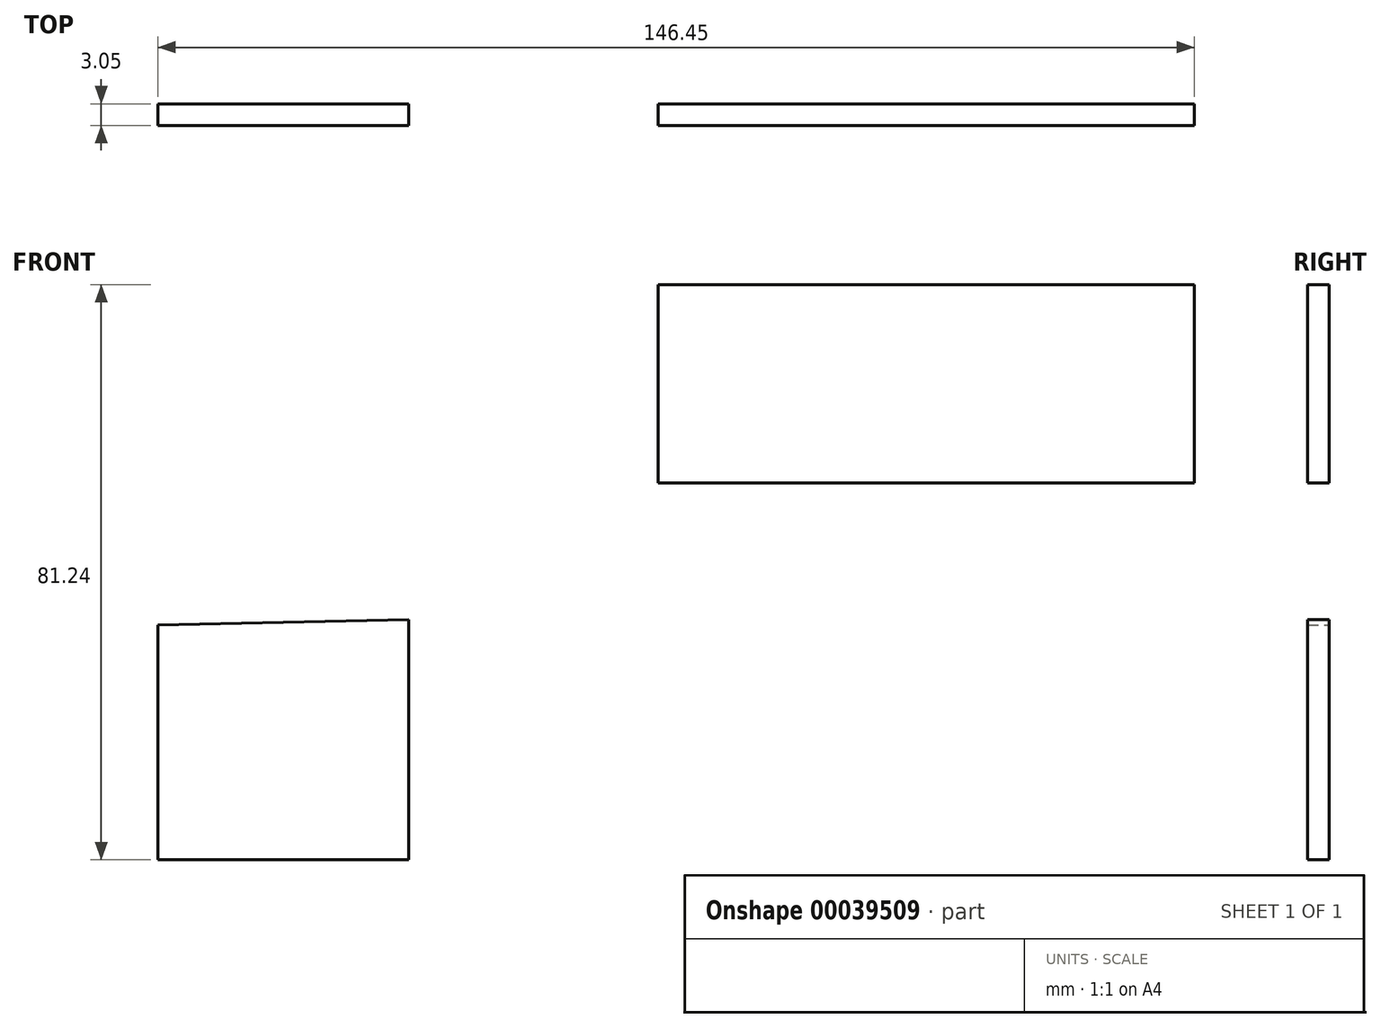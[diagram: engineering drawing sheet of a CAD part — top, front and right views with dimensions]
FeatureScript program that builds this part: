
annotation { "Feature Type Name" : "Feature", "Feature Type Description" : "" }
export const myFeature = defineFeature(function(context is Context, id is Id, definition is map)
    precondition{}
    {
        {
            var Q0;
            Q0=qCreatedBy(makeId("Front.planeOp"),FACE);
            var sketch = newSketch(context, id + "F0", { "sketchPlane" : qUnion([Q0])});
            skLineSegment(sketch, "E0", {"start": v(0, 0) * mm, "end": v(0, 27.99) * mm});
            skLineSegment(sketch, "E1", {"start": v(0, 27.99) * mm, "end": v(75.77, 27.99) * mm});
            skLineSegment(sketch, "E2", {"start": v(75.77, 27.99) * mm, "end": v(75.77, 0) * mm});
            skLineSegment(sketch, "E3", {"start": v(75.77, 0) * mm, "end": v(0, 0) * mm});
            skLineSegment(sketch, "E4", {"start": v(0, 14) * mm, "end": v(75.77, 14) * mm});
            skLineSegment(sketch, "E5", {"start": v(37.88, 27.99) * mm, "end": v(37.88, 0) * mm});
            skSolve(sketch);
        }
        {
            var Q0;
            Q0 = qSketchRegion(id + "F0", true);
            extrude(context, id + "F1", {"entities" : qUnion([Q0]), "depth" : 3.05 * mm});
        }
        {
            var Q0;
            Q0=qCreatedBy(makeId("Front.planeOp"),FACE);
            var sketch = newSketch(context, id + "F2", { "sketchPlane" : qUnion([Q0])});
            skLineSegment(sketch, "E6", {"start": v(-70.68, -20.07) * mm, "end": v(-70.68, -53.25) * mm});
            skLineSegment(sketch, "E7", {"start": v(-70.68, -53.25) * mm, "end": v(-35.25, -53.25) * mm});
            skLineSegment(sketch, "E8", {"start": v(-35.25, -53.25) * mm, "end": v(-35.25, -19.32) * mm});
            skLineSegment(sketch, "E9", {"start": v(-35.25, -19.32) * mm, "end": v(-70.68, -20.07) * mm});
            skSolve(sketch);
        }
        {
            var Q0;
            Q0 = qSketchRegion(id + "F2", true);
            extrude(context, id + "F3", {"entities" : qUnion([Q0]), "depth" : 3.05 * mm});
        }
    });
